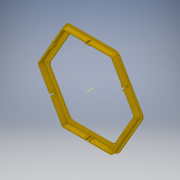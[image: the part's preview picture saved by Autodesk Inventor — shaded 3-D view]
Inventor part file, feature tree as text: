
AUTODESK INVENTOR PART (.ipt)
format: ipt  version: 2019 (Build 230136000, 136)  size: 276,992 bytes
history: native  units: mm
features: extrude x6, sketch x6, projected_geometry x3, fillet x2, other x1, pattern_circular x1
ambient origin geometry x8: Origin, YZ Plane, XZ Plane, XY Plane, X Axis, Y Axis, Z Axis, Center Point
bodies: Solid1 (feature_tree)
feature tree (19):
  extrude  "Extrusion1"  Depth=2.0mm
  extrude  "Extrusion5"  Depth=3.0mm
  extrude  "Extrusion6"  Depth=10.0mm
  fillet  "Fillet1"  [1 undecoded]
  fillet  "Fillet2"  Radius=8.0mm
  extrude  "Extrusion7"  TaperAngle=0.0deg  [1 undecoded]
  extrude  "Extrusion8"  Depth=4.0mm
  other  "Work Axis2"
  pattern_circular  "Circular Pattern1"  [2 undecoded]
  extrude  "Extrusion9"  Depth=7.5mm
  sketch  "Sketch1"  dims[d0=175.0mm d1=2.0mm]
  sketch  "Sketch5"  dims[d2=0.0mm d15=3.0mm]
  projected_geometry  "Projected Loop4"
  sketch  "Sketch7"  dims[d16=2.0mm d17=10.0mm d18=0.0mm d19=8.0mm]
  projected_geometry  "Projected Loop6"
  sketch  "Sketch8"  dims[d20=7.0mm d21=0.0mm]
  sketch  "Sketch9"  dims[d22=10.0mm d23=4.0mm]
  projected_geometry  "Projected Loop7"
  sketch  "Sketch11"  dims[d24=10.0mm d25=3.3mm d26=7.5mm d27=0.0mm d28=4.0mm d29=3.0mm d30=5.0mm d31=0.0mm d32=60.0mm d33=360.0deg d35=1.0mm d36=3.0mm d37=0.5mm d38=0.0mm]
note: 4 required parameter values undecoded (feature->parameter linkage not recoverable at this tier; creation-order binding heuristic only, values carry confidence <= 0.55)
